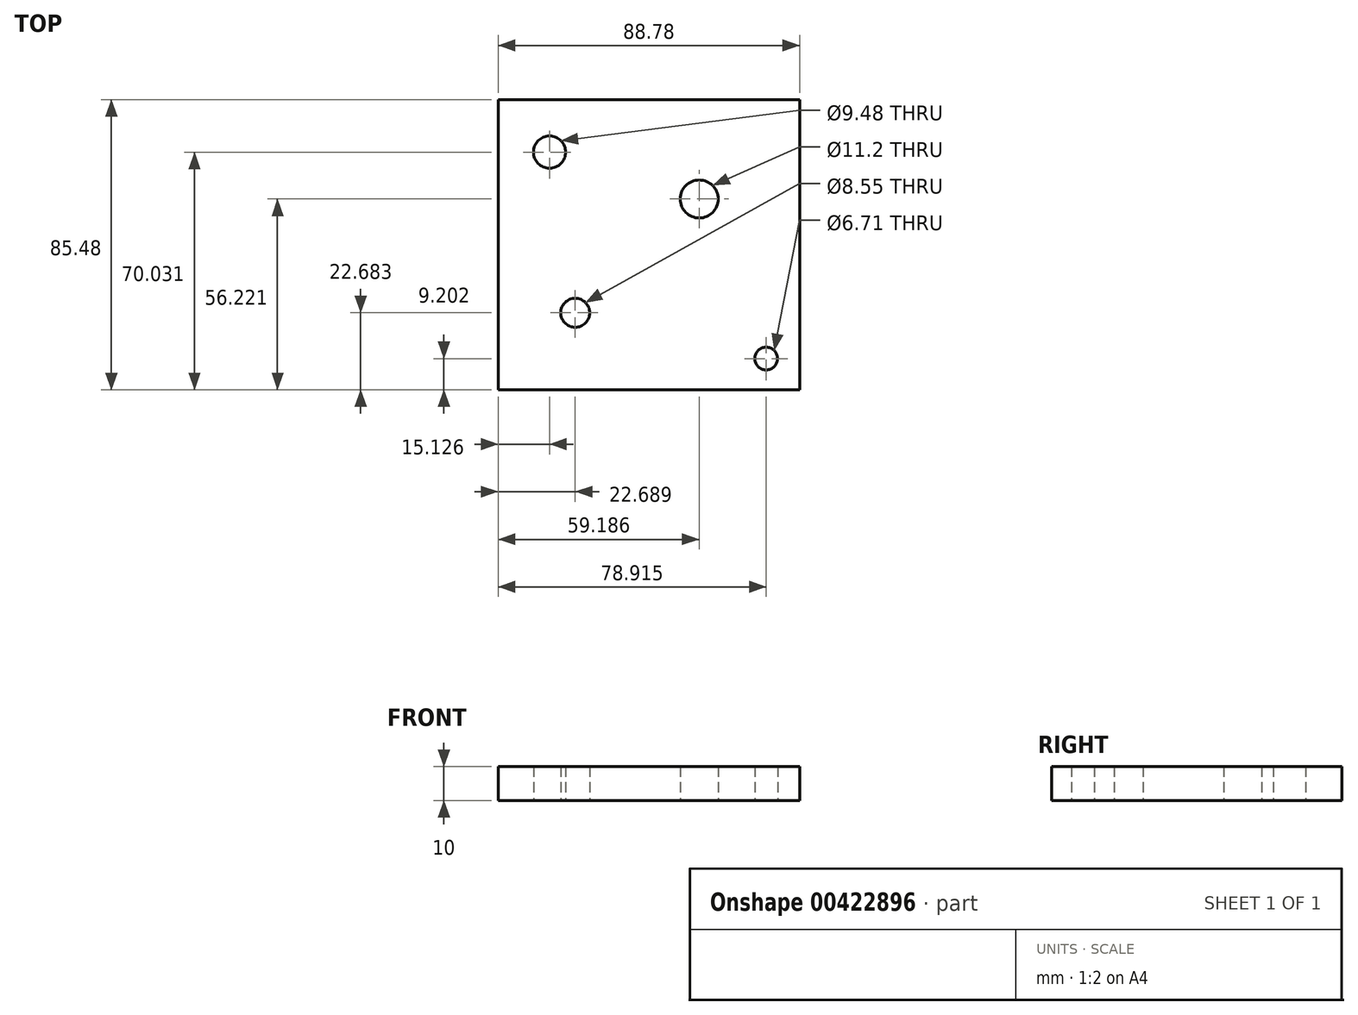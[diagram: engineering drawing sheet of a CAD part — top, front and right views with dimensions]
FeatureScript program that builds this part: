
annotation { "Feature Type Name" : "Feature", "Feature Type Description" : "" }
export const myFeature = defineFeature(function(context is Context, id is Id, definition is map)
    precondition{}
    {
        {
            var Q0;
            Q0=qCreatedBy(makeId("Top.planeOp"),FACE);
            var sketch = newSketch(context, id + "F0", { "sketchPlane" : qUnion([Q0])});
            skLineSegment(sketch, "E0.bottom", {"start": v(44.39, -42.74) * mm, "end": v(-44.39, -42.74) * mm});
            skLineSegment(sketch, "E0.top", {"start": v(44.39, 42.74) * mm, "end": v(-44.39, 42.74) * mm});
            skLineSegment(sketch, "E0.left", {"start": v(44.39, -42.74) * mm, "end": v(44.39, 42.74) * mm});
            skLineSegment(sketch, "E0.right", {"start": v(-44.39, -42.74) * mm, "end": v(-44.39, 42.74) * mm});
            skPoint(sketch, "E0.middle", {"position": v(0, 0) * mm});
            skCircle(sketch, "E1", {"center": v(-29.26, 27.3) * mm, "radius": 4.74 * mm});
            skCircle(sketch, "E2", {"center": v(14.8, 13.48) * mm, "radius": 5.6 * mm});
            skCircle(sketch, "E3", {"center": v(-21.7, -20.06) * mm, "radius": 4.27 * mm});
            skCircle(sketch, "E4", {"center": v(34.52, -33.54) * mm, "radius": 3.35 * mm});
            skSolve(sketch);
        }
        {
            var Q0;
            Q0 = qSketchRegion(id + "F0", true);
            extrude(context, id + "F1", {"entities" : qUnion([Q0]), "depth" : 10 * mm});
        }
    });
